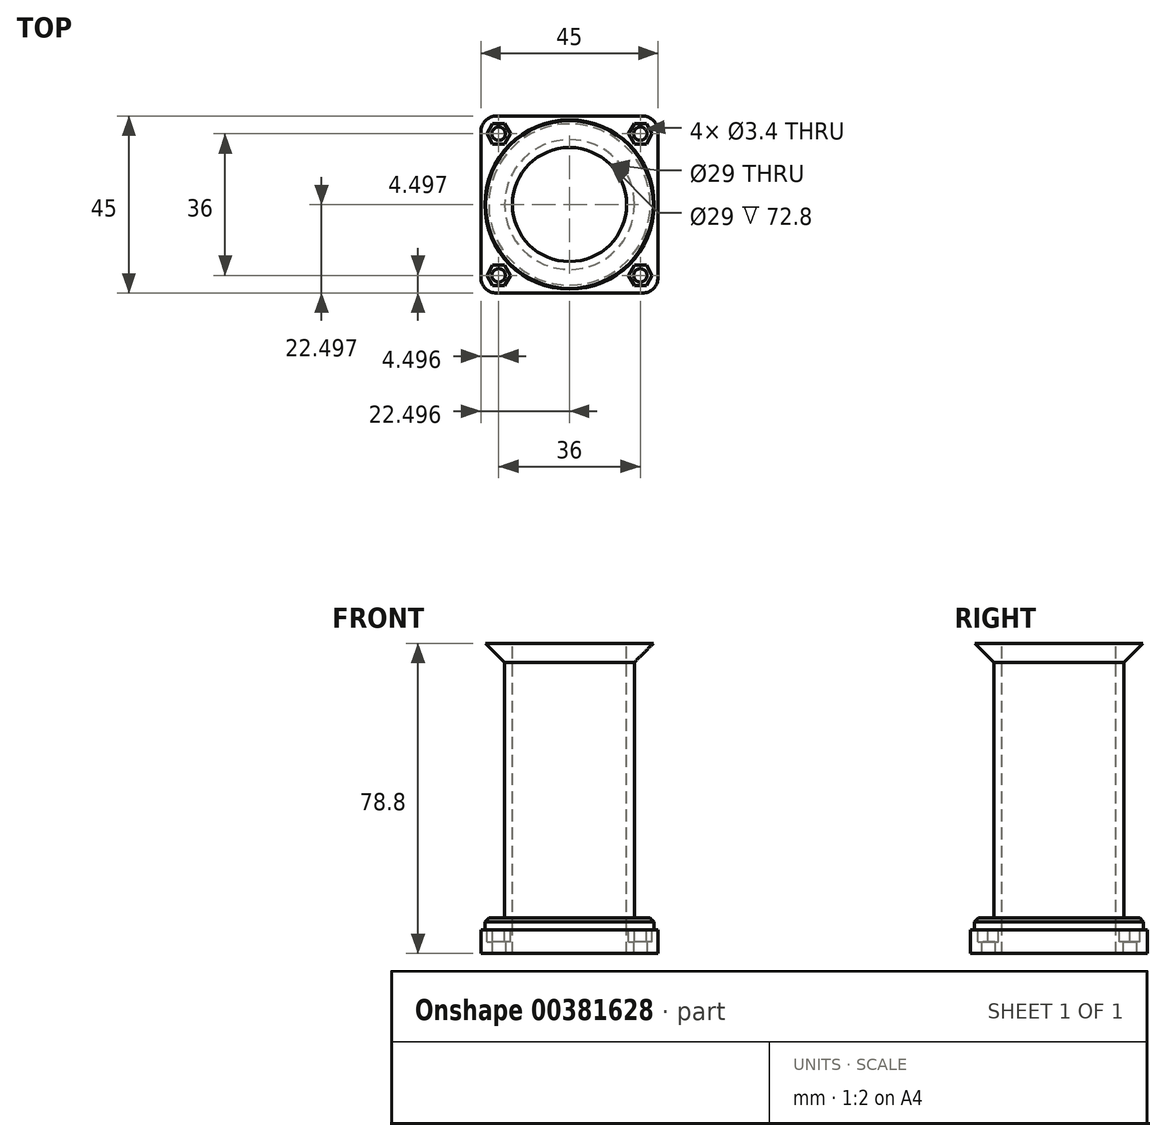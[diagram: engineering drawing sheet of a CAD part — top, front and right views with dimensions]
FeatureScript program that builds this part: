
annotation { "Feature Type Name" : "Feature", "Feature Type Description" : "" }
export const myFeature = defineFeature(function(context is Context, id is Id, definition is map)
    precondition{}
    {
        {
            var Q0;
            Q0=qCreatedBy(makeId("Top.planeOp"),FACE);
            var sketch = newSketch(context, id + "F0", { "sketchPlane" : qUnion([Q0])});
            skLineSegment(sketch, "E0.bottom", {"start": v(-14.7, -16.1) * mm, "end": v(30.3, -16.1) * mm});
            skLineSegment(sketch, "E0.top", {"start": v(-14.7, 28.9) * mm, "end": v(30.3, 28.9) * mm});
            skLineSegment(sketch, "E0.left", {"start": v(-14.7, -16.1) * mm, "end": v(-14.7, 28.9) * mm});
            skLineSegment(sketch, "E0.right", {"start": v(30.3, -16.1) * mm, "end": v(30.3, 28.9) * mm});
            skLineSegment(sketch, "E1.bottom", {"start": v(-10.2, -11.6) * mm, "end": v(25.8, -11.6) * mm, "construction": true});
            skLineSegment(sketch, "E1.top", {"start": v(-10.2, 24.4) * mm, "end": v(25.8, 24.4) * mm, "construction": true});
            skLineSegment(sketch, "E1.left", {"start": v(-10.2, -11.6) * mm, "end": v(-10.2, 24.4) * mm, "construction": true});
            skLineSegment(sketch, "E1.right", {"start": v(25.8, -11.6) * mm, "end": v(25.8, 24.4) * mm, "construction": true});
            skCircle(sketch, "E2", {"center": v(-10.2, 24.4) * mm, "radius": 1.7 * mm});
            skCircle(sketch, "E3", {"center": v(25.8, 24.4) * mm, "radius": 1.7 * mm});
            skCircle(sketch, "E4", {"center": v(25.8, -11.6) * mm, "radius": 1.7 * mm});
            skCircle(sketch, "E5", {"center": v(-10.2, -11.6) * mm, "radius": 1.7 * mm});
            skSolve(sketch);
        }
        {
            var Q0;
            Q0 = qSketchRegion(id + "F0", true);
            extrude(context, id + "F1", {"entities" : qUnion([Q0]), "depth" : 6 * mm});
        }
        {
            var Q0;
            Q0=makeQuery(id+"F1.opExtrude","CAP_FACE",FACE,{"disambiguationData":[OSD([sQuery(id+"F0.wireOp",EDGE,"E0.bottom"),sQuery(id+"F0.wireOp",EDGE,"E0.top"),sQuery(id+"F0.wireOp",EDGE,"E0.left"),sQuery(id+"F0.wireOp",EDGE,"E0.right"),sQuery(id+"F0.wireOp",EDGE,"E2"),sQuery(id+"F0.wireOp",EDGE,"E3"),sQuery(id+"F0.wireOp",EDGE,"E4"),sQuery(id+"F0.wireOp",EDGE,"E5")])],"isStart":false});
            var sketch = newSketch(context, id + "F2", { "sketchPlane" : qUnion([Q0])});
            skCircle(sketch, "E6.0", {"center": v(-10.2, 24.4) * mm, "radius": 1.7 * mm});
            skCircle(sketch, "E6.1", {"center": v(25.8, 24.4) * mm, "radius": 1.7 * mm});
            skCircle(sketch, "E6.2", {"center": v(25.8, -11.6) * mm, "radius": 1.7 * mm});
            skCircle(sketch, "E6.3", {"center": v(-10.2, -11.6) * mm, "radius": 1.7 * mm});
            skLineSegment(sketch, "E7", {"start": v(-10.2, 24.4) * mm, "end": v(25.8, 24.4) * mm, "construction": true});
            skLineSegment(sketch, "E8", {"start": v(25.8, -11.6) * mm, "end": v(-10.2, -11.6) * mm, "construction": true});
            skLineSegment(sketch, "E9", {"start": v(-10.2, 24.4) * mm, "end": v(-10.2, -11.6) * mm, "construction": true});
            skLineSegment(sketch, "E10", {"start": v(25.8, -11.6) * mm, "end": v(25.8, 24.4) * mm, "construction": true});
            skCircle(sketch, "E11.cCircle", {"center": v(-10.2, 24.4) * mm, "radius": 2.6 * mm, "construction": true});
            skLineSegment(sketch, "E11.0", {"start": v(-8.7, 21.8) * mm, "end": v(-11.7, 21.8) * mm});
            skLineSegment(sketch, "E11.1", {"start": v(-11.7, 21.8) * mm, "end": v(-13.2, 24.4) * mm});
            skLineSegment(sketch, "E11.2", {"start": v(-13.2, 24.4) * mm, "end": v(-11.7, 27) * mm});
            skLineSegment(sketch, "E11.3", {"start": v(-11.7, 27) * mm, "end": v(-8.7, 27) * mm});
            skLineSegment(sketch, "E11.4", {"start": v(-8.7, 27) * mm, "end": v(-7.2, 24.4) * mm});
            skLineSegment(sketch, "E11.5", {"start": v(-7.2, 24.4) * mm, "end": v(-8.7, 21.8) * mm});
            skPoint(sketch, "E11.0.midPoint", {"position": v(-10.2, 21.8) * mm});
            skCircle(sketch, "E12.cCircle", {"center": v(25.8, 24.4) * mm, "radius": 2.6 * mm, "construction": true});
            skLineSegment(sketch, "E12.0", {"start": v(27.3, 21.8) * mm, "end": v(24.3, 21.8) * mm});
            skLineSegment(sketch, "E12.1", {"start": v(24.3, 21.8) * mm, "end": v(22.8, 24.4) * mm});
            skLineSegment(sketch, "E12.2", {"start": v(22.8, 24.4) * mm, "end": v(24.3, 27) * mm});
            skLineSegment(sketch, "E12.3", {"start": v(24.3, 27) * mm, "end": v(27.3, 27) * mm});
            skLineSegment(sketch, "E12.4", {"start": v(27.3, 27) * mm, "end": v(28.8, 24.4) * mm});
            skLineSegment(sketch, "E12.5", {"start": v(28.8, 24.4) * mm, "end": v(27.3, 21.8) * mm});
            skPoint(sketch, "E12.0.midPoint", {"position": v(25.8, 21.8) * mm});
            skCircle(sketch, "E13.cCircle", {"center": v(-10.2, -11.6) * mm, "radius": 2.6 * mm, "construction": true});
            skLineSegment(sketch, "E13.0", {"start": v(-11.7, -9) * mm, "end": v(-8.7, -9) * mm});
            skLineSegment(sketch, "E13.1", {"start": v(-8.7, -9) * mm, "end": v(-7.2, -11.6) * mm});
            skLineSegment(sketch, "E13.2", {"start": v(-7.2, -11.6) * mm, "end": v(-8.7, -14.2) * mm});
            skLineSegment(sketch, "E13.3", {"start": v(-8.7, -14.2) * mm, "end": v(-11.7, -14.2) * mm});
            skLineSegment(sketch, "E13.4", {"start": v(-11.7, -14.2) * mm, "end": v(-13.2, -11.6) * mm});
            skLineSegment(sketch, "E13.5", {"start": v(-13.2, -11.6) * mm, "end": v(-11.7, -9) * mm});
            skPoint(sketch, "E13.0.midPoint", {"position": v(-10.2, -9) * mm});
            skCircle(sketch, "E14.cCircle", {"center": v(25.8, -11.6) * mm, "radius": 2.6 * mm, "construction": true});
            skLineSegment(sketch, "E14.0", {"start": v(24.3, -9) * mm, "end": v(27.3, -9) * mm});
            skLineSegment(sketch, "E14.1", {"start": v(27.3, -9) * mm, "end": v(28.8, -11.6) * mm});
            skLineSegment(sketch, "E14.2", {"start": v(28.8, -11.6) * mm, "end": v(27.3, -14.2) * mm});
            skLineSegment(sketch, "E14.3", {"start": v(27.3, -14.2) * mm, "end": v(24.3, -14.2) * mm});
            skLineSegment(sketch, "E14.4", {"start": v(24.3, -14.2) * mm, "end": v(22.8, -11.6) * mm});
            skLineSegment(sketch, "E14.5", {"start": v(22.8, -11.6) * mm, "end": v(24.3, -9) * mm});
            skPoint(sketch, "E14.0.midPoint", {"position": v(25.8, -9) * mm});
            skSolve(sketch);
        }
        {
            var Q0;
            Q0 = qSketchRegion(id + "F2", true);
            extrude(context, id + "F3", {"entities" : qUnion([Q0]), "operationType" : NewBodyOperationType.REMOVE, "oppositeDirection" : true, "depth" : 3 * mm});
        }
        {
            var Q0;
            Q0=makeQuery(id+"F1.opExtrude","SWEPT_EDGE",EDGE,{"disambiguationData":[OSD([sQuery(id+"F0.wireOp",EDGE,"E0.top"),sQuery(id+"F0.wireOp",EDGE,"E0.left")])]});
            var Q1;
            Q1=makeQuery(id+"F1.opExtrude","SWEPT_EDGE",EDGE,{"disambiguationData":[OSD([sQuery(id+"F0.wireOp",EDGE,"E0.top"),sQuery(id+"F0.wireOp",EDGE,"E0.right")])]});
            var Q2;
            Q2=makeQuery(id+"F1.opExtrude","SWEPT_EDGE",EDGE,{"disambiguationData":[OSD([sQuery(id+"F0.wireOp",EDGE,"E0.bottom"),sQuery(id+"F0.wireOp",EDGE,"E0.right")])]});
            var Q3;
            Q3=makeQuery(id+"F1.opExtrude","SWEPT_EDGE",EDGE,{"disambiguationData":[OSD([sQuery(id+"F0.wireOp",EDGE,"E0.bottom"),sQuery(id+"F0.wireOp",EDGE,"E0.left")])]});
            fillet(context, id + "F4", {"entities" : qUnion([Q0, Q1, Q2, Q3]), "radius" : 4 * mm, "tangentPropagation" : true, "allowEdgeOverflow" : false});
        }
        {
            var Q0;
            Q0=makeQuery(id+"F1.opExtrude","CAP_FACE",FACE,{"disambiguationData":[OSD([sQuery(id+"F0.wireOp",EDGE,"E0.bottom"),sQuery(id+"F0.wireOp",EDGE,"E0.top"),sQuery(id+"F0.wireOp",EDGE,"E0.left"),sQuery(id+"F0.wireOp",EDGE,"E0.right"),sQuery(id+"F0.wireOp",EDGE,"E2"),sQuery(id+"F0.wireOp",EDGE,"E3"),sQuery(id+"F0.wireOp",EDGE,"E4"),sQuery(id+"F0.wireOp",EDGE,"E5")])],"isStart":false});
            var sketch = newSketch(context, id + "F5", { "sketchPlane" : qUnion([Q0])});
            skLineSegment(sketch, "E15", {"start": v(7.8, 28.9) * mm, "end": v(7.8, -16.1) * mm, "construction": true});
            skLineSegment(sketch, "E16", {"start": v(-14.7, 6.4) * mm, "end": v(30.3, 6.4) * mm, "construction": true});
            skCircle(sketch, "E17", {"center": v(7.8, 6.4) * mm, "radius": 21.5 * mm});
            skSolve(sketch);
        }
        {
            var Q0;
            Q0=makeQuery(id+"F5.imprint","IMPRINT",FACE,{"disambiguationData":[TD([[makeQuery(id+"F5.imprint","IMPRINT",EDGE,{"derivedFrom":sQuery(id+"F5.wireOp",EDGE,"E17")}),1.0]])]});
            var Q1;
            Q1=sQuery(id+"F5.wireOp",EDGE,"E17");
            extrude(context, id + "F6", {"entities" : qUnion([Q0]), "surfaceEntities" : qUnion([Q1]), "depth" : 3 * mm});
        }
        {
            var Q0;
            Q0=makeQuery(id+"F6.opExtrude","CAP_EDGE",EDGE,{"disambiguationData":[OSD([sQuery(id+"F5.wireOp",EDGE,"E17")])],"isStart":false});
            chamfer(context, id + "F7", {"entities" : qUnion([Q0]), "width" : 1 * mm, "tangentPropagation" : true});
        }
        {
            var Q0;
            Q0=makeQuery(id+"F6.opExtrude","CAP_FACE",FACE,{"disambiguationData":[OSD([sQuery(id+"F5.wireOp",EDGE,"E17")])],"isStart":false});
            var sketch = newSketch(context, id + "F8", { "sketchPlane" : qUnion([Q0])});
            skCircle(sketch, "E18", {"center": v(7.8, 6.4) * mm, "radius": 16.5 * mm});
            skSolve(sketch);
        }
        {
            var Q0;
            Q0=makeQuery(id+"F8.imprint","IMPRINT",FACE,{"disambiguationData":[TD([[makeQuery(id+"F8.imprint","IMPRINT",EDGE,{"derivedFrom":sQuery(id+"F8.wireOp",EDGE,"E18")}),1.0]])]});
            extrude(context, id + "F9", {"entities" : qUnion([Q0]), "operationType" : NewBodyOperationType.ADD, "depth" : 65 * mm});
        }
        {
            var Q0;
            Q0=makeQuery(id+"F9.opExtrude","CAP_FACE",FACE,{"disambiguationData":[OSD([sQuery(id+"F8.wireOp",EDGE,"E18")])],"isStart":false});
            var sketch = newSketch(context, id + "F10", { "sketchPlane" : qUnion([Q0])});
            skCircle(sketch, "E19", {"center": v(7.8, 6.4) * mm, "radius": 21.5 * mm});
            skSolve(sketch);
        }
        {
            var Q0;
            Q0 = qSketchRegion(id + "F10", true);
            extrude(context, id + "F11", {"entities" : qUnion([Q0]), "operationType" : NewBodyOperationType.ADD, "depth" : 4.8 * mm});
        }
        {
            var Q0;
            Q0=makeQuery(id+"F11.opExtrude","CAP_EDGE",EDGE,{"disambiguationData":[OSD([sQuery(id+"F10.wireOp",EDGE,"E19")])],"isStart":true});
            chamfer(context, id + "F12", {"entities" : qUnion([Q0]), "width" : 5 * mm, "tangentPropagation" : true});
        }
        {
            var Q0;
            Q0=makeQuery(id+"F11.opExtrude","CAP_FACE",FACE,{"disambiguationData":[OSD([sQuery(id+"F10.wireOp",EDGE,"E19")])],"isStart":false});
            var sketch = newSketch(context, id + "F13", { "sketchPlane" : qUnion([Q0])});
            skCircle(sketch, "E20", {"center": v(7.8, 6.4) * mm, "radius": 14.5 * mm});
            skCircle(sketch, "E21.0", {"center": v(7.8, 6.4) * mm, "radius": 16.5 * mm});
            skSolve(sketch);
        }
        {
            var Q0;
            Q0=makeQuery(id+"F13.imprint","IMPRINT",FACE,{"disambiguationData":[TD([[makeQuery(id+"F13.imprint","IMPRINT",EDGE,{"derivedFrom":sQuery(id+"F13.wireOp",EDGE,"E20")}),1.0]])]});
            extrude(context, id + "F14", {"entities" : qUnion([Q0]), "operationType" : NewBodyOperationType.REMOVE, "oppositeDirection" : true, "depth" : 100 * mm});
        }
    });
